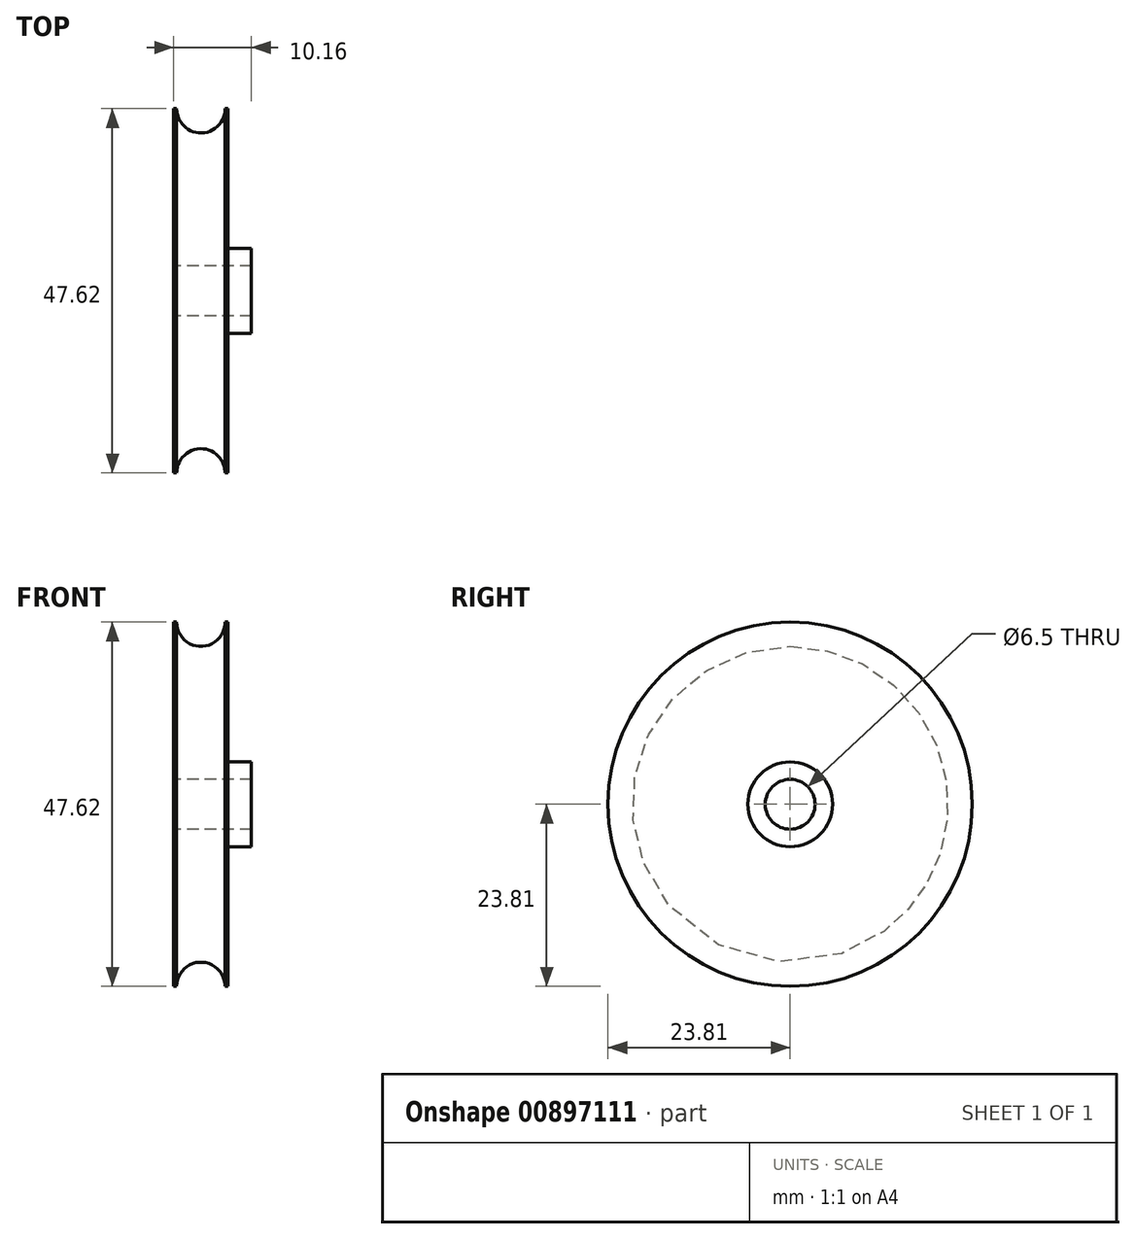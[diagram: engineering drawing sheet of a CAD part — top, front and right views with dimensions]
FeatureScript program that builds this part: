
annotation { "Feature Type Name" : "Feature", "Feature Type Description" : "" }
export const myFeature = defineFeature(function(context is Context, id is Id, definition is map)
    precondition{}
    {
        {
            var Q0;
            Q0=qCreatedBy(makeId("Front.planeOp"),FACE);
            var sketch = newSketch(context, id + "F0", { "sketchPlane" : qUnion([Q0])});
            skLineSegment(sketch, "E0", {"start": v(0, 0) * mm, "end": v(12.14, 0) * mm, "construction": true});
            skLineSegment(sketch, "E1", {"start": v(0, 3.25) * mm, "end": v(10.16, 3.25) * mm});
            skLineSegment(sketch, "E2", {"start": v(10.16, 3.25) * mm, "end": v(10.16, 5.54) * mm});
            skLineSegment(sketch, "E3", {"start": v(10.16, 5.54) * mm, "end": v(7.11, 5.54) * mm});
            skLineSegment(sketch, "E4", {"start": v(7.11, 5.54) * mm, "end": v(7.11, 23.81) * mm});
            skLineSegment(sketch, "E5", {"start": v(0, 3.25) * mm, "end": v(0, 23.81) * mm});
            skLineSegment(sketch, "E6", {"start": v(0, 23.81) * mm, "end": v(0.38, 23.81) * mm});
            skLineSegment(sketch, "E7", {"start": v(7.11, 23.81) * mm, "end": v(6.73, 23.81) * mm});
            skArc(sketch, "E8", {"start": v(0.38, 23.81) * mm, "mid": v(3.56, 20.64) * mm, "end": v(6.73, 23.81) * mm});
            skSolve(sketch);
        }
        {
            var Q0;
            Q0=qSketchRegion(id+"F0",true);
            var Q1;
            Q1=sQuery(id+"F0.wireOp",EDGE,"E0");
            revolve(context, id + "F1", {"entities" : qUnion([Q0]), "axis" : qUnion([Q1]), "revolveType" : RevolveType.FULL});
        }
    });
